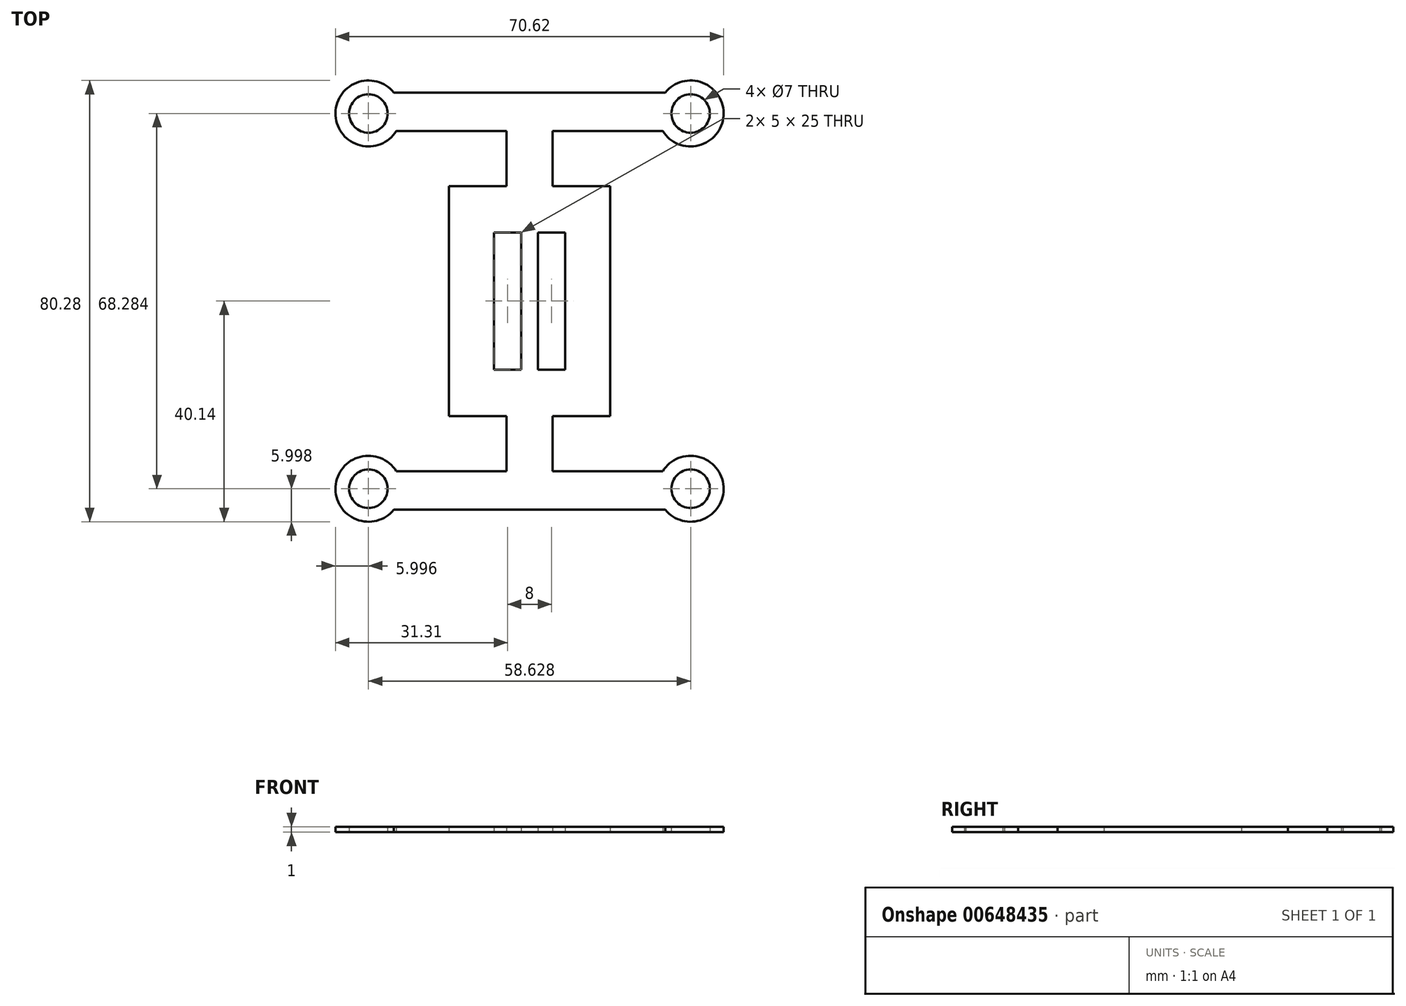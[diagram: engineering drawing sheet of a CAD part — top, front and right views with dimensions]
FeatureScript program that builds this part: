
annotation { "Feature Type Name" : "Feature", "Feature Type Description" : "" }
export const myFeature = defineFeature(function(context is Context, id is Id, definition is map)
    precondition{}
    {
        {
            var Q0;
            Q0=qCreatedBy(makeId("Top.planeOp"),FACE);
            var sketch = newSketch(context, id + "F0", { "sketchPlane" : qUnion([Q0])});
            skLineSegment(sketch, "E0.bottom", {"start": v(-29.31, 34.14) * mm, "end": v(29.31, 34.14) * mm, "construction": true});
            skLineSegment(sketch, "E0.top", {"start": v(-29.31, -34.14) * mm, "end": v(29.31, -34.14) * mm, "construction": true});
            skLineSegment(sketch, "E0.left", {"start": v(-29.31, 34.14) * mm, "end": v(-29.31, -34.14) * mm, "construction": true});
            skLineSegment(sketch, "E0.right", {"start": v(29.31, 34.14) * mm, "end": v(29.31, -34.14) * mm, "construction": true});
            skPoint(sketch, "E0.middle", {"position": v(0, 0) * mm});
            skLineSegment(sketch, "E1", {"start": v(0, 49.78) * mm, "end": v(0, 0) * mm, "construction": true});
            skLineSegment(sketch, "E2", {"start": v(0, 0) * mm, "end": v(52.54, 0) * mm, "construction": true});
            skCircle(sketch, "E3", {"center": v(29.31, 34.14) * mm, "radius": 3.5 * mm});
            skCircle(sketch, "E4", {"center": v(29.31, 34.14) * mm, "radius": 6 * mm});
            skLineSegment(sketch, "E5", {"start": v(0, 37.95) * mm, "end": v(24.67, 37.95) * mm});
            skLineSegment(sketch, "E6", {"start": v(24.24, 30.95) * mm, "end": v(4.22, 30.95) * mm});
            skLineSegment(sketch, "E7", {"start": v(4.22, 30.95) * mm, "end": v(4.22, 20.95) * mm});
            skLineSegment(sketch, "E8", {"start": v(4.22, 20.95) * mm, "end": v(14.65, 20.95) * mm});
            skLineSegment(sketch, "E9", {"start": v(14.65, 20.95) * mm, "end": v(14.65, 0) * mm});
            skLineSegment(sketch, "E10.MirrorCS", {"start": v(-14.65, 20.95) * mm, "end": v(-14.65, 0) * mm});
            skLineSegment(sketch, "E11.MirrorCS", {"start": v(-4.22, 20.95) * mm, "end": v(-14.65, 20.95) * mm});
            skLineSegment(sketch, "E12.MirrorCS", {"start": v(-4.22, 30.95) * mm, "end": v(-4.22, 20.95) * mm});
            skLineSegment(sketch, "E13.MirrorCS", {"start": v(0, 37.95) * mm, "end": v(-24.67, 37.95) * mm});
            skLineSegment(sketch, "E14.MirrorCS", {"start": v(-24.24, 30.95) * mm, "end": v(-4.22, 30.95) * mm});
            skCircle(sketch, "E15.MirrorC", {"center": v(-29.31, 34.14) * mm, "radius": 6 * mm});
            skCircle(sketch, "E16.MirrorC", {"center": v(-29.31, 34.14) * mm, "radius": 3.5 * mm});
            skLineSegment(sketch, "E17.MirrorCS", {"start": v(0, -37.95) * mm, "end": v(-24.67, -37.95) * mm});
            skCircle(sketch, "E18.MirrorC", {"center": v(29.31, -34.14) * mm, "radius": 3.5 * mm});
            skLineSegment(sketch, "E19.MirrorCS", {"start": v(0, -37.95) * mm, "end": v(24.67, -37.95) * mm});
            skLineSegment(sketch, "E20.MirrorCS", {"start": v(29.31, -34.14) * mm, "end": v(29.31, 34.14) * mm, "construction": true});
            skLineSegment(sketch, "E21.MirrorCS", {"start": v(14.65, -20.95) * mm, "end": v(14.65, 0) * mm});
            skLineSegment(sketch, "E22.MirrorCS", {"start": v(4.22, -20.95) * mm, "end": v(14.65, -20.95) * mm});
            skLineSegment(sketch, "E23.MirrorCS", {"start": v(24.24, -30.95) * mm, "end": v(4.22, -30.95) * mm});
            skCircle(sketch, "E24.MirrorC", {"center": v(29.31, -34.14) * mm, "radius": 6 * mm});
            skLineSegment(sketch, "E25.MirrorCS", {"start": v(4.22, -30.95) * mm, "end": v(4.22, -20.95) * mm});
            skLineSegment(sketch, "E26.MirrorCS", {"start": v(-14.65, -20.95) * mm, "end": v(-14.65, 0) * mm});
            skLineSegment(sketch, "E27.MirrorCS", {"start": v(-24.24, -30.95) * mm, "end": v(-4.22, -30.95) * mm});
            skCircle(sketch, "E28.MirrorC", {"center": v(-29.31, -34.14) * mm, "radius": 3.5 * mm});
            skCircle(sketch, "E29.MirrorC", {"center": v(-29.31, -34.14) * mm, "radius": 6 * mm});
            skLineSegment(sketch, "E30.MirrorCS", {"start": v(-4.22, -20.95) * mm, "end": v(-14.65, -20.95) * mm});
            skLineSegment(sketch, "E31.MirrorCS", {"start": v(-4.22, -30.95) * mm, "end": v(-4.22, -20.95) * mm});
            skLineSegment(sketch, "E32.bottom", {"start": v(-6.5, 12.5) * mm, "end": v(-1.5, 12.5) * mm});
            skLineSegment(sketch, "E32.top", {"start": v(-6.5, -12.5) * mm, "end": v(-1.5, -12.5) * mm});
            skLineSegment(sketch, "E32.left", {"start": v(-6.5, 12.5) * mm, "end": v(-6.5, -12.5) * mm});
            skLineSegment(sketch, "E32.right", {"start": v(-1.5, 12.5) * mm, "end": v(-1.5, -12.5) * mm});
            skPoint(sketch, "E32.middle", {"position": v(-4, 0) * mm});
            skLineSegment(sketch, "E33.MirrorCS", {"start": v(6.5, 12.5) * mm, "end": v(6.5, -12.5) * mm});
            skPoint(sketch, "E34.MirrorP", {"position": v(4, 0) * mm});
            skLineSegment(sketch, "E35.MirrorCS", {"start": v(6.5, -12.5) * mm, "end": v(1.5, -12.5) * mm});
            skLineSegment(sketch, "E36.MirrorCS", {"start": v(1.5, 12.5) * mm, "end": v(1.5, -12.5) * mm});
            skLineSegment(sketch, "E37.MirrorCS", {"start": v(6.5, 12.5) * mm, "end": v(1.5, 12.5) * mm});
            skSolve(sketch);
        }
        {
            var Q0;
            Q0 = qSketchRegion(id + "F0", true);
            extrude(context, id + "F1", {"entities" : qUnion([Q0]), "depth" : 1 * mm, "offsetDistance" : 25 * mm});
        }
    });
